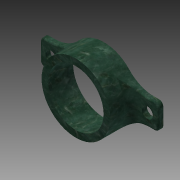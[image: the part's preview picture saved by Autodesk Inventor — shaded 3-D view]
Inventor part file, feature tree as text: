
AUTODESK INVENTOR PART (.ipt)
format: ipt  version: 2014 (Build 180170000, 170)  size: 240,640 bytes
history: native  units: in
note: dims shown in document units (in); Inventor stores cm internally (conversion verified against a paired STEP export)
features: sketch x5, extrude x5, fillet x4, plane x2, reference x1, projected_geometry x1
ambient origin geometry x8: Origin, YZ Plane, XZ Plane, XY Plane, X Axis, Y Axis, Z Axis, Center Point
bodies: Solid1 (feature_tree)
feature tree (18):
  plane  "Work Plane1"
  sketch  "Sketch1"  dims[d0=0.01in d1=0.1in]
  plane  "Work Plane2"
  extrude  "Extrusion1"  Depth=0.1in
  sketch  "Sketch2"  dims[d2=1.0in d3=0.0in d4=0.1in d7=0.75in d8=0.75in d9=0.75in]
  extrude  "Extrusion3"  Depth=0.1in
  fillet  "Fillet1"  Radius=0.75in
  fillet  "Fillet2"  Radius=0.75in
  fillet  "Fillet3"  Radius=0.75in
  extrude  "Extrusion4"  Depth=0.15in TaperAngle=0.0deg
  extrude  "Extrusion5"  Depth=0.25in
  extrude  "Extrusion6"  Depth=0.33in
  fillet  "Fillet4"  Radius=0.33in
  reference  "Reference1"
  sketch  "Sketch3"  dims[d10=0.375in d11=0.15in d12=0.0in]
  sketch  "Sketch4"  dims[d13=1.0in d14=0.25in]
  projected_geometry  "Projected Loop1"
  sketch  "Sketch5"  dims[d15=0.125in d16=0.33in d17=0.33in d18=0.33in d19=0.15in d20=0.0in d21=0.2in d22=0.0in d23=0.1in d24=0.1in d25=0.0in d26=0.05in]
